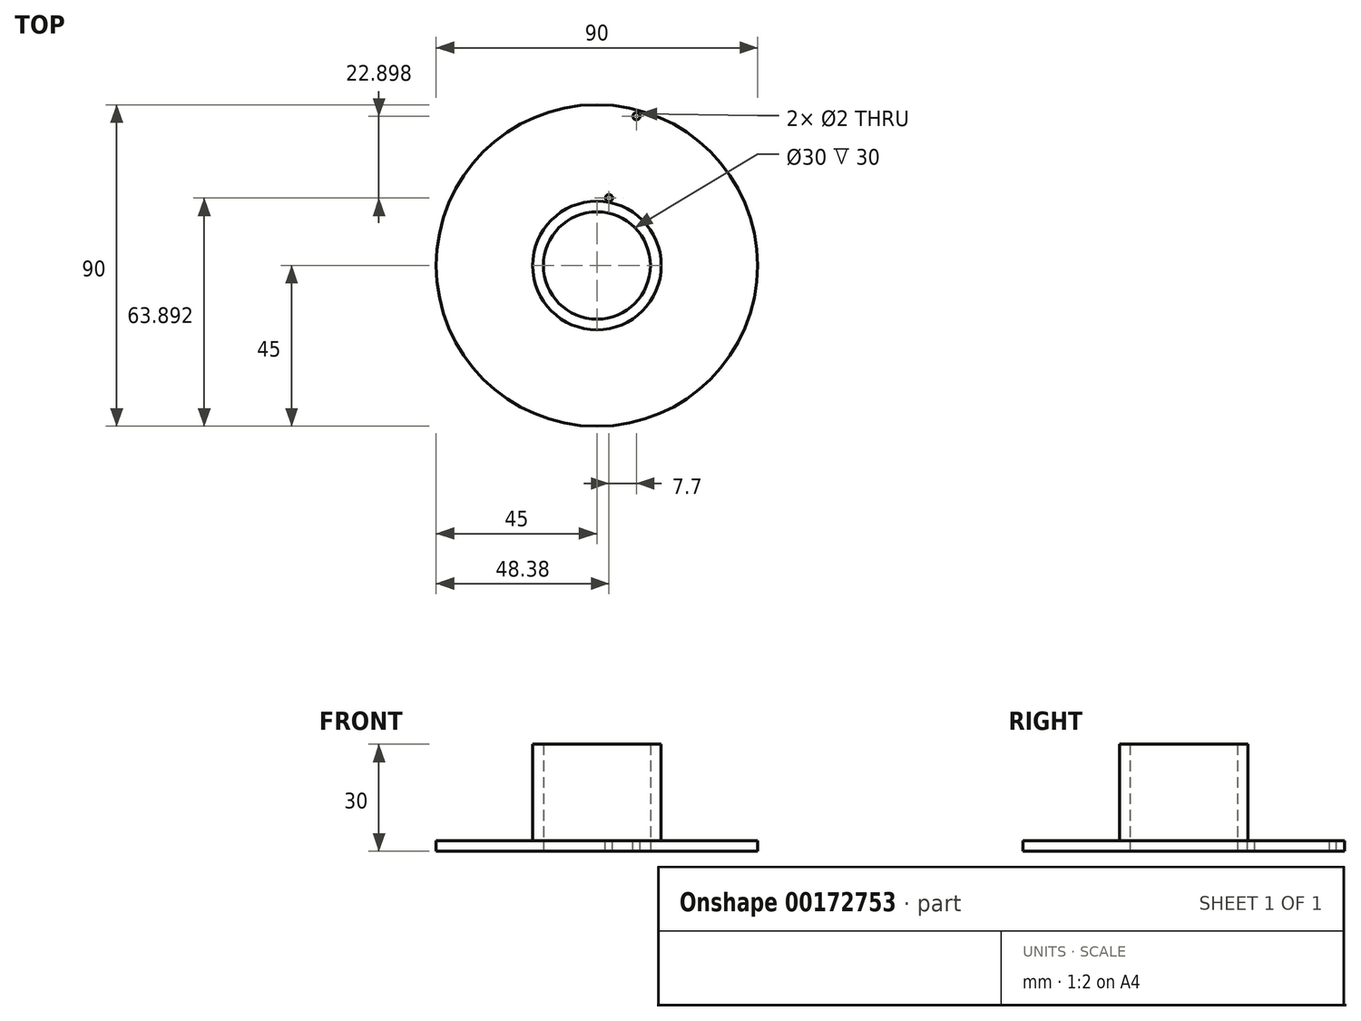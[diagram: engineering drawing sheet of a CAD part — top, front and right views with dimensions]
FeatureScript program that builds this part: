
annotation { "Feature Type Name" : "Feature", "Feature Type Description" : "" }
export const myFeature = defineFeature(function(context is Context, id is Id, definition is map)
    precondition{}
    {
        {
            var Q0;
            Q0=qCreatedBy(makeId("Top.planeOp"),FACE);
            var sketch = newSketch(context, id + "F0", { "sketchPlane" : qUnion([Q0])});
            skCircle(sketch, "E0", {"center": v(0, 0) * mm, "radius": 15 * mm});
            skCircle(sketch, "E1", {"center": v(0, 0) * mm, "radius": 45 * mm});
            skCircle(sketch, "E2", {"center": v(0, 0) * mm, "radius": 18 * mm});
            skSolve(sketch);
        }
        {
            var Q0;
            Q0=makeQuery(id+"F0.imprint","IMPRINT",FACE,{"disambiguationData":[TD([[makeQuery(id+"F0.imprint","IMPRINT",EDGE,{"derivedFrom":sQuery(id+"F0.wireOp",EDGE,"E0")}),-1.0]])]});
            extrude(context, id + "F1", {"entities" : qUnion([Q0]), "depth" : 30 * mm});
        }
        {
            var Q0;
            Q0 = qSketchRegion(id + "F0", true);
            extrude(context, id + "F2", {"entities" : qUnion([Q0]), "operationType" : NewBodyOperationType.ADD, "depth" : 3 * mm});
        }
        {
            var Q0;
            Q0=makeQuery(id+"F2.opExtrude","CAP_FACE",FACE,{"disambiguationData":[OSD([sQuery(id+"F0.wireOp",EDGE,"E1"),sQuery(id+"F0.wireOp",EDGE,"E2")])],"isStart":false});
            var sketch = newSketch(context, id + "F3", { "sketchPlane" : qUnion([Q0])});
            skCircle(sketch, "E3", {"center": v(3.38, 18.9) * mm, "radius": 1 * mm});
            skCircle(sketch, "E4", {"center": v(11.08, 41.79) * mm, "radius": 1 * mm});
            skSolve(sketch);
        }
        {
            var Q0;
            Q0=makeQuery(id+"F3.imprint","IMPRINT",FACE,{"disambiguationData":[TD([[makeQuery(id+"F3.imprint","IMPRINT",EDGE,{"derivedFrom":sQuery(id+"F3.wireOp",EDGE,"E3")}),1.0]])]});
            extrude(context, id + "F4", {"entities" : qUnion([Q0]), "operationType" : NewBodyOperationType.REMOVE, "oppositeDirection" : true, "depth" : 32.8 * mm});
        }
        {
            var Q0;
            Q0 = qSketchRegion(id + "F3", true);
            extrude(context, id + "F5", {"entities" : qUnion([Q0]), "operationType" : NewBodyOperationType.REMOVE, "oppositeDirection" : true, "depth" : 25 * mm});
        }
    });
